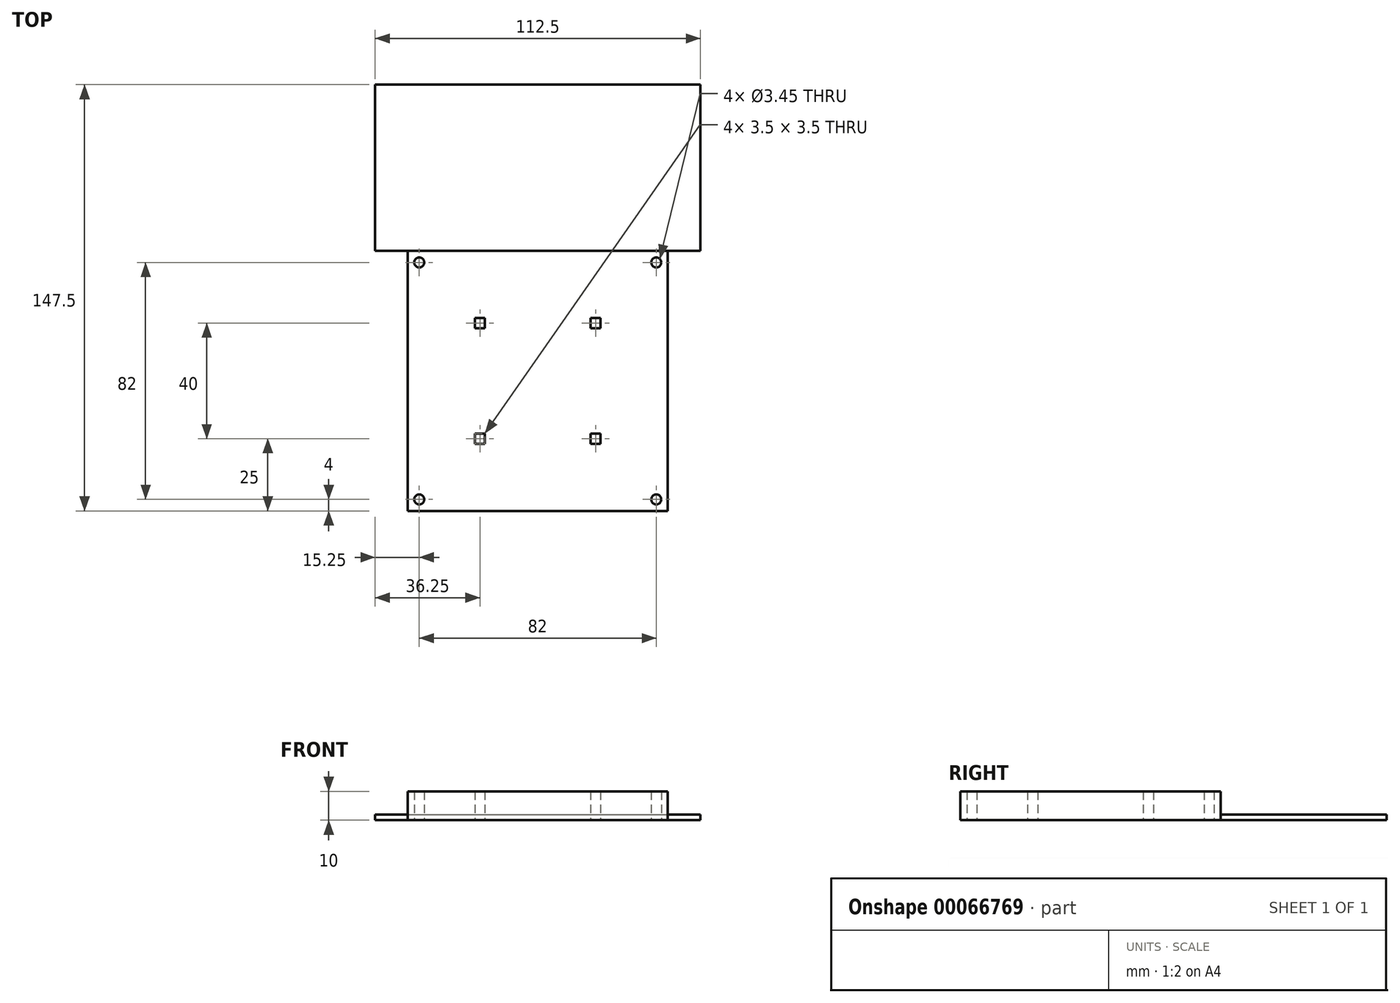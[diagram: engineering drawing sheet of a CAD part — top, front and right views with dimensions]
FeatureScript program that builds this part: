
annotation { "Feature Type Name" : "Feature", "Feature Type Description" : "" }
export const myFeature = defineFeature(function(context is Context, id is Id, definition is map)
    precondition{}
    {
        {
            var Q0;
            Q0=qCreatedBy(makeId("Top.planeOp"),FACE);
            var sketch = newSketch(context, id + "F0", { "sketchPlane" : qUnion([Q0])});
            skLineSegment(sketch, "E0", {"start": v(45, 0) * mm, "end": v(45, 45) * mm});
            skLineSegment(sketch, "E1", {"start": v(45, 45) * mm, "end": v(0, 45) * mm});
            skLineSegment(sketch, "E2", {"start": v(41, 41) * mm, "end": v(41, 45) * mm, "construction": true});
            skLineSegment(sketch, "E3", {"start": v(41, 41) * mm, "end": v(45, 41) * mm, "construction": true});
            skCircle(sketch, "E4", {"center": v(41, 41) * mm, "radius": 1.73 * mm});
            skLineSegment(sketch, "E5.MirrorCS", {"start": v(-41, 41) * mm, "end": v(-45, 41) * mm, "construction": true});
            skLineSegment(sketch, "E6.MirrorCS", {"start": v(-41, 41) * mm, "end": v(-41, 45) * mm, "construction": true});
            skCircle(sketch, "E7.MirrorC", {"center": v(-41, 41) * mm, "radius": 1.73 * mm});
            skLineSegment(sketch, "E8.MirrorCS", {"start": v(-45, 45) * mm, "end": v(0, 45) * mm});
            skLineSegment(sketch, "E9.MirrorCS", {"start": v(-45, 0) * mm, "end": v(-45, 45) * mm});
            skCircle(sketch, "E10.MirrorC", {"center": v(-41, -41) * mm, "radius": 1.73 * mm});
            skLineSegment(sketch, "E11.MirrorCS", {"start": v(-41, -41) * mm, "end": v(-41, -45) * mm, "construction": true});
            skLineSegment(sketch, "E12.MirrorCS", {"start": v(41, -41) * mm, "end": v(45, -41) * mm, "construction": true});
            skLineSegment(sketch, "E13.MirrorCS", {"start": v(41, -41) * mm, "end": v(41, -45) * mm, "construction": true});
            skLineSegment(sketch, "E14.MirrorCS", {"start": v(-41, -41) * mm, "end": v(-45, -41) * mm, "construction": true});
            skLineSegment(sketch, "E15.MirrorCS", {"start": v(-45, 0) * mm, "end": v(-45, -45) * mm});
            skLineSegment(sketch, "E16.MirrorCS", {"start": v(-45, -45) * mm, "end": v(0, -45) * mm});
            skLineSegment(sketch, "E17.MirrorCS", {"start": v(45, 0) * mm, "end": v(45, -45) * mm});
            skLineSegment(sketch, "E18.MirrorCS", {"start": v(45, -45) * mm, "end": v(0, -45) * mm});
            skCircle(sketch, "E19.MirrorC", {"center": v(41, -41) * mm, "radius": 1.73 * mm});
            skLineSegment(sketch, "E20", {"start": v(45, -20) * mm, "end": v(20, -20) * mm, "construction": true});
            skLineSegment(sketch, "E21", {"start": v(20, -20) * mm, "end": v(-20, -20) * mm, "construction": true});
            skLineSegment(sketch, "E22", {"start": v(-20, -20) * mm, "end": v(-45, -20) * mm, "construction": true});
            skLineSegment(sketch, "E23", {"start": v(-20, -20) * mm, "end": v(-20, 20) * mm, "construction": true});
            skLineSegment(sketch, "E24", {"start": v(-20, 20) * mm, "end": v(20, 20) * mm, "construction": true});
            skLineSegment(sketch, "E25", {"start": v(20, 20) * mm, "end": v(20, -20) * mm, "construction": true});
            skLineSegment(sketch, "E26.rect.bottom", {"start": v(-18.25, 18.25) * mm, "end": v(-21.75, 18.25) * mm});
            skLineSegment(sketch, "E26.rect.top", {"start": v(-18.25, 21.75) * mm, "end": v(-21.75, 21.75) * mm});
            skLineSegment(sketch, "E26.rect.left", {"start": v(-18.25, 18.25) * mm, "end": v(-18.25, 21.75) * mm});
            skLineSegment(sketch, "E26.rect.right", {"start": v(-21.75, 18.25) * mm, "end": v(-21.75, 21.75) * mm});
            skPoint(sketch, "E26.rect.middle", {"position": v(-20, 20) * mm});
            skLineSegment(sketch, "E27.MirrorCS", {"start": v(18.25, 18.25) * mm, "end": v(18.25, 21.75) * mm});
            skLineSegment(sketch, "E28.MirrorCS", {"start": v(18.25, 21.75) * mm, "end": v(21.75, 21.75) * mm});
            skLineSegment(sketch, "E29.MirrorCS", {"start": v(18.25, 18.25) * mm, "end": v(21.75, 18.25) * mm});
            skLineSegment(sketch, "E30.MirrorCS", {"start": v(21.75, 18.25) * mm, "end": v(21.75, 21.75) * mm});
            skLineSegment(sketch, "E31.MirrorCS", {"start": v(-18.25, -21.75) * mm, "end": v(-21.75, -21.75) * mm});
            skLineSegment(sketch, "E32.MirrorCS", {"start": v(-21.75, -18.25) * mm, "end": v(-21.75, -21.75) * mm});
            skLineSegment(sketch, "E33.MirrorCS", {"start": v(-18.25, -18.25) * mm, "end": v(-21.75, -18.25) * mm});
            skLineSegment(sketch, "E34.MirrorCS", {"start": v(-18.25, -18.25) * mm, "end": v(-18.25, -21.75) * mm});
            skLineSegment(sketch, "E35.MirrorCS", {"start": v(18.25, -18.25) * mm, "end": v(18.25, -21.75) * mm});
            skLineSegment(sketch, "E36.MirrorCS", {"start": v(18.25, -18.25) * mm, "end": v(21.75, -18.25) * mm});
            skLineSegment(sketch, "E37.MirrorCS", {"start": v(18.25, -21.75) * mm, "end": v(21.75, -21.75) * mm});
            skLineSegment(sketch, "E38.MirrorCS", {"start": v(21.75, -18.25) * mm, "end": v(21.75, -21.75) * mm});
            skSolve(sketch);
        }
        {
            var Q0;
            Q0=qSketchRegion(id+"F0",true);
            extrude(context, id + "F1", {"entities" : qUnion([Q0]), "depth" : 10 * mm});
        }
        {
            var Q0;
            Q0=qCreatedBy(makeId("Top.planeOp"),FACE);
            var sketch = newSketch(context, id + "F2", { "sketchPlane" : qUnion([Q0])});
            skLineSegment(sketch, "E39", {"start": v(45, 45) * mm, "end": v(45, 102.5) * mm, "construction": true});
            skLineSegment(sketch, "E40", {"start": v(-45, 45) * mm, "end": v(-45, 102.5) * mm, "construction": true});
            skLineSegment(sketch, "E41", {"start": v(-45, 102.5) * mm, "end": v(45, 102.5) * mm});
            skLineSegment(sketch, "E42", {"start": v(45, 102.5) * mm, "end": v(56.25, 102.5) * mm});
            skLineSegment(sketch, "E43", {"start": v(-45, 102.5) * mm, "end": v(-56.25, 102.5) * mm});
            skLineSegment(sketch, "E44", {"start": v(-56.25, 102.5) * mm, "end": v(-56.25, 45) * mm});
            skLineSegment(sketch, "E45", {"start": v(56.25, 102.5) * mm, "end": v(56.25, 45) * mm});
            skLineSegment(sketch, "E46", {"start": v(-56.25, 45) * mm, "end": v(56.25, 45) * mm});
            skSolve(sketch);
        }
        {
            var Q0;
            Q0=qSketchRegion(id+"F2",true);
            extrude(context, id + "F3", {"entities" : qUnion([Q0]), "operationType" : NewBodyOperationType.ADD, "depth" : 2 * mm});
        }
    });
